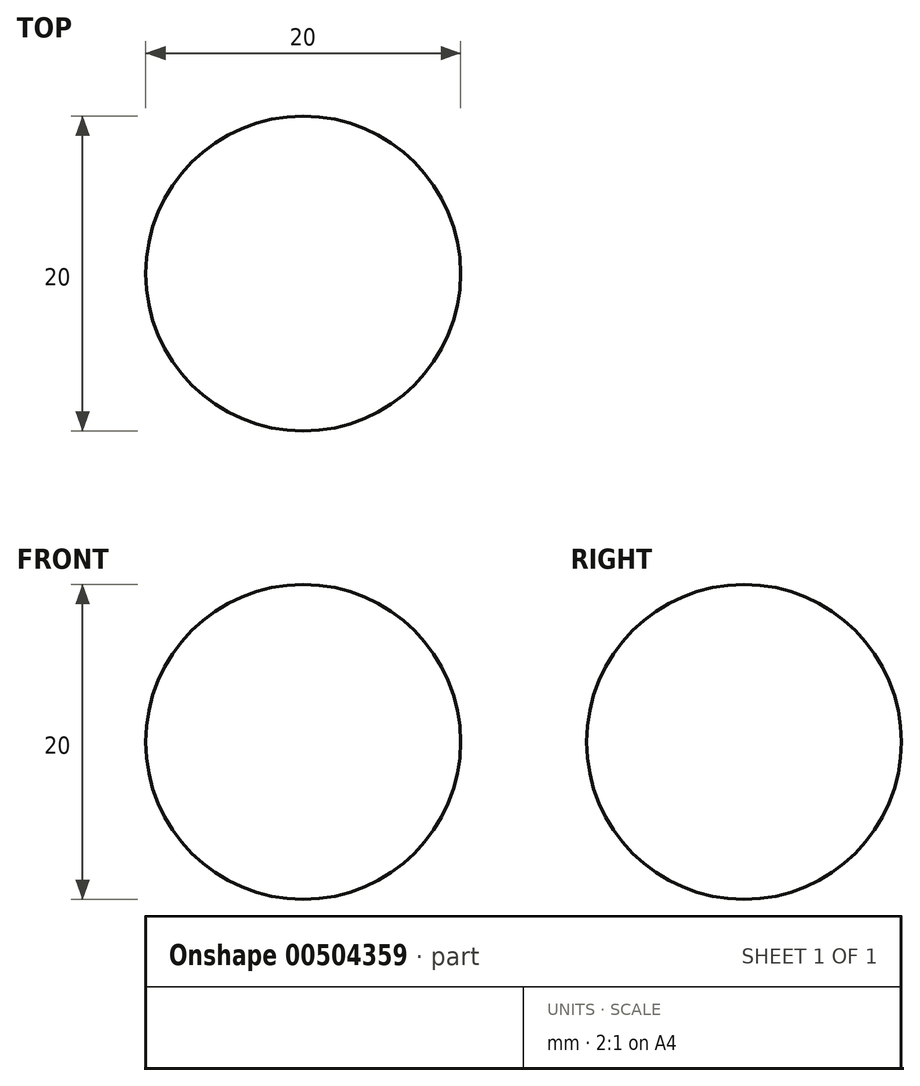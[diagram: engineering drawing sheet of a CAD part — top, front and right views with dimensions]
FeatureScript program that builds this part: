
annotation { "Feature Type Name" : "Feature", "Feature Type Description" : "" }
export const myFeature = defineFeature(function(context is Context, id is Id, definition is map)
    precondition{}
    {
        {
            var Q0;
            Q0=qCreatedBy(makeId("Front.planeOp"),FACE);
            var sketch = newSketch(context, id + "F0", { "sketchPlane" : qUnion([Q0])});
            skLineSegment(sketch, "E0", {"start": v(0, 29.05) * mm, "end": v(0, -33.42) * mm, "construction": true});
            skArc(sketch, "E1", {"start": v(0, -10) * mm, "mid": v(10, 0) * mm, "end": v(0, 10) * mm});
            skLineSegment(sketch, "E2", {"start": v(0, 10) * mm, "end": v(0, -10) * mm});
            skSolve(sketch);
        }
        {
            var Q0;
            Q0=makeQuery(id+"F0.imprint","IMPRINT",FACE,{"disambiguationData":[TD([[makeQuery(id+"F0.imprint","IMPRINT",EDGE,{"derivedFrom":sQuery(id+"F0.wireOp",EDGE,"E1")}),1.0]])]});
            var Q1;
            Q1=sQuery(id+"F0.wireOp",EDGE,"E2");
            revolve(context, id + "F1", {"entities" : qUnion([Q0]), "axis" : qUnion([Q1]), "revolveType" : RevolveType.FULL});
        }
    });
